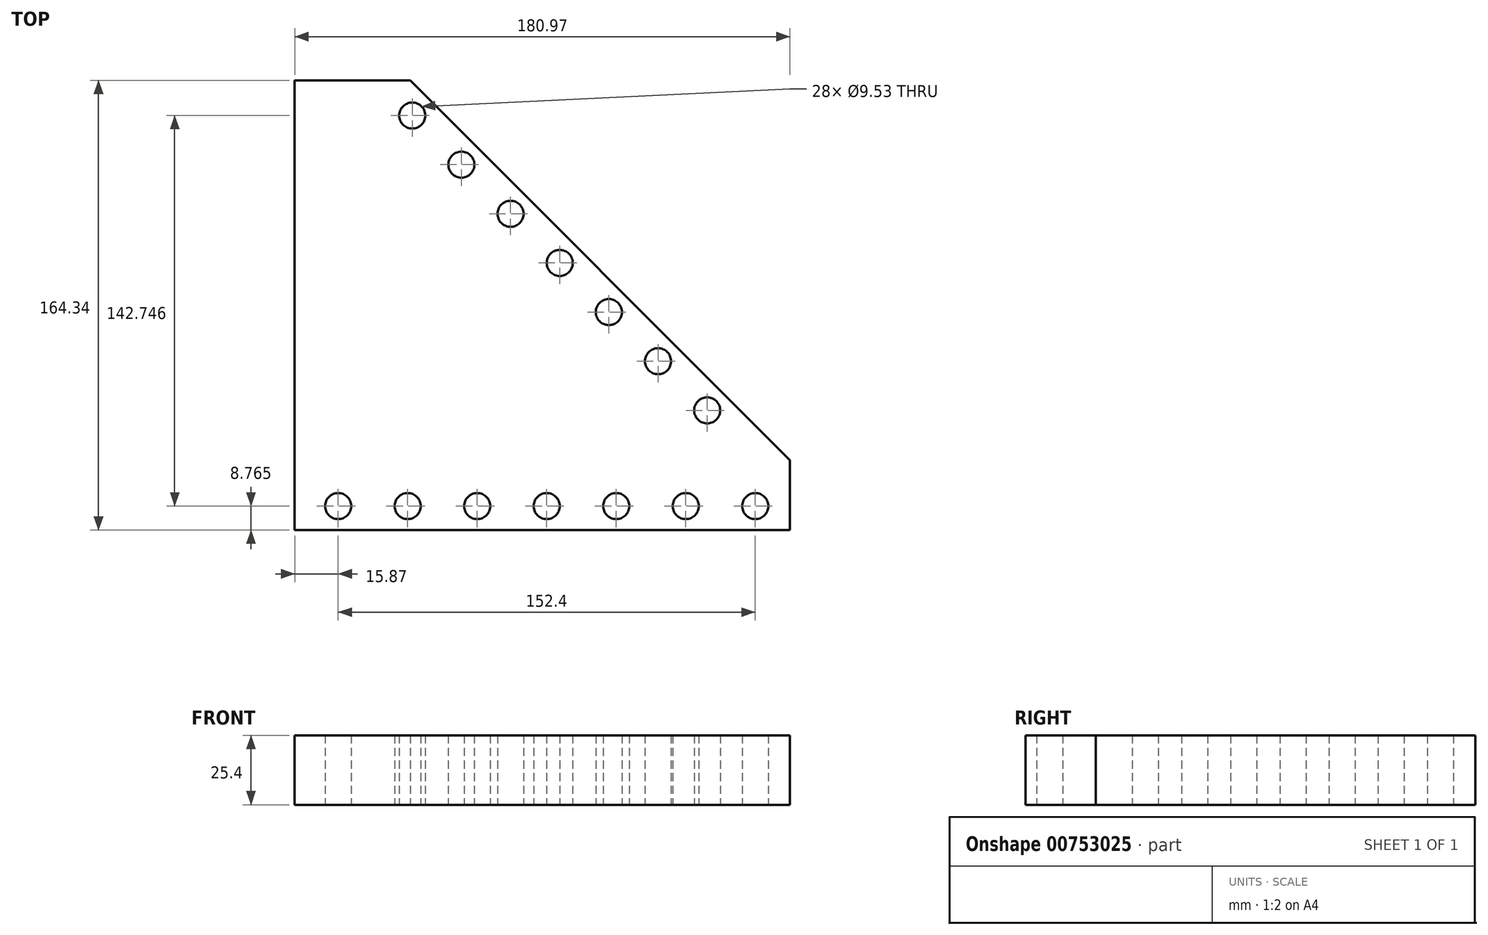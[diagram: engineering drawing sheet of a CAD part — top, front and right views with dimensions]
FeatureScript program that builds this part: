
annotation { "Feature Type Name" : "Feature", "Feature Type Description" : "" }
export const myFeature = defineFeature(function(context is Context, id is Id, definition is map)
    precondition{}
    {
        {
            var Q0;
            Q0=qCreatedBy(makeId("Top.planeOp"),FACE);
            var sketch = newSketch(context, id + "F0", { "sketchPlane" : qUnion([Q0])});
            skLineSegment(sketch, "E0.bottom", {"start": v(0, 0) * mm, "end": v(-304.8, 0) * mm});
            skLineSegment(sketch, "E0.top", {"start": v(0, 19.05) * mm, "end": v(-304.8, 19.05) * mm});
            skLineSegment(sketch, "E0.left", {"start": v(0, 0) * mm, "end": v(0, 19.05) * mm});
            skLineSegment(sketch, "E0.right", {"start": v(-304.8, 0) * mm, "end": v(-304.8, 19.05) * mm});
            skCircle(sketch, "E1", {"center": v(-25.4, 9.52) * mm, "radius": 4.76 * mm});
            skCircle(sketch, "E2.1.0.0", {"center": v(-50.8, 9.52) * mm, "radius": 4.76 * mm});
            skCircle(sketch, "E2.2.0.0", {"center": v(-76.2, 9.52) * mm, "radius": 4.76 * mm});
            skCircle(sketch, "E2.3.0.0", {"center": v(-101.6, 9.52) * mm, "radius": 4.76 * mm});
            skCircle(sketch, "E2.4.0.0", {"center": v(-127, 9.52) * mm, "radius": 4.76 * mm});
            skCircle(sketch, "E2.5.0.0", {"center": v(-152.4, 9.52) * mm, "radius": 4.76 * mm});
            skCircle(sketch, "E2.6.0.0", {"center": v(-177.8, 9.52) * mm, "radius": 4.76 * mm});
            skCircle(sketch, "E2.7.0.0", {"center": v(-203.2, 9.52) * mm, "radius": 4.76 * mm});
            skCircle(sketch, "E2.8.0.0", {"center": v(-228.6, 9.52) * mm, "radius": 4.76 * mm});
            skCircle(sketch, "E2.9.0.0", {"center": v(-254, 9.52) * mm, "radius": 4.76 * mm});
            skCircle(sketch, "E2.10.0.0", {"center": v(-279.4, 9.52) * mm, "radius": 4.76 * mm});
            skLineSegment(sketch, "E2.direction1", {"start": v(-25.4, 9.52) * mm, "end": v(-50.8, 9.52) * mm, "construction": true});
            skLineSegment(sketch, "E3.bottom", {"start": v(-57.15, 19.81) * mm, "end": v(-272.68, 235.34) * mm});
            skLineSegment(sketch, "E3.top", {"start": v(-43.68, 33.28) * mm, "end": v(-259.2, 248.8) * mm});
            skLineSegment(sketch, "E3.left", {"start": v(-57.15, 19.81) * mm, "end": v(-43.68, 33.28) * mm});
            skLineSegment(sketch, "E3.right", {"start": v(-272.68, 235.34) * mm, "end": v(-259.2, 248.8) * mm});
            skCircle(sketch, "E4", {"center": v(-68.38, 44.5) * mm, "radius": 4.76 * mm});
            skCircle(sketch, "E5.1.0.0", {"center": v(-86.34, 62.47) * mm, "radius": 4.76 * mm});
            skCircle(sketch, "E5.2.0.0", {"center": v(-104.3, 80.43) * mm, "radius": 4.76 * mm});
            skCircle(sketch, "E5.3.0.0", {"center": v(-122.26, 98.39) * mm, "radius": 4.76 * mm});
            skCircle(sketch, "E5.4.0.0", {"center": v(-140.22, 116.35) * mm, "radius": 4.76 * mm});
            skCircle(sketch, "E5.5.0.0", {"center": v(-158.18, 134.31) * mm, "radius": 4.76 * mm});
            skCircle(sketch, "E5.6.0.0", {"center": v(-176.14, 152.27) * mm, "radius": 4.76 * mm});
            skCircle(sketch, "E5.7.0.0", {"center": v(-194.1, 170.23) * mm, "radius": 4.76 * mm});
            skCircle(sketch, "E5.8.0.0", {"center": v(-212.06, 188.2) * mm, "radius": 4.76 * mm});
            skCircle(sketch, "E5.9.0.0", {"center": v(-230.02, 206.15) * mm, "radius": 4.76 * mm});
            skCircle(sketch, "E5.10.0.0", {"center": v(-247.98, 224.11) * mm, "radius": 4.76 * mm});
            skLineSegment(sketch, "E5.direction1", {"start": v(-68.38, 44.5) * mm, "end": v(-86.34, 62.47) * mm, "construction": true});
            skLineSegment(sketch, "E6.0", {"start": v(-75.11, 37.77) * mm, "end": v(-57.15, 19.81) * mm, "construction": true});
            skLineSegment(sketch, "E6.1", {"start": v(-75.11, 37.77) * mm, "end": v(-68.38, 44.5) * mm, "construction": true});
            skLineSegment(sketch, "E7", {"start": v(-38.1, 0.76) * mm, "end": v(-38.1, 26.33) * mm});
            skLineSegment(sketch, "E8", {"start": v(-219.08, 0.76) * mm, "end": v(-219.08, 165.1) * mm});
            skLineSegment(sketch, "E9", {"start": v(-219.08, 165.1) * mm, "end": v(-176.87, 165.1) * mm});
            skLineSegment(sketch, "E10", {"start": v(-219.08, 0.76) * mm, "end": v(-38.1, 0.76) * mm});
            skPoint(sketch, "E11.orphan", {"position": v(-219.08, 0) * mm});
            skPoint(sketch, "E12.orphan", {"position": v(-38.1, 0) * mm});
            skLineSegment(sketch, "E13", {"start": v(-176.87, 165.1) * mm, "end": v(-38.1, 26.33) * mm});
            skLineSegment(sketch, "E14", {"start": v(-219.08, 0.76) * mm, "end": v(-115.8, 104.03) * mm});
            skLineSegment(sketch, "E15", {"start": v(-146.95, 109.61) * mm, "end": v(-133.48, 123.08) * mm});
            skLineSegment(sketch, "E16", {"start": v(-43.68, 33.28) * mm, "end": v(-133.57, 123) * mm});
            skSolve(sketch);
        }
        {
            var Q0;
            {var subQ0=sQuery(id+"F0.wireOp",EDGE,"E8");var subQ1=sQuery(id+"F0.wireOp",EDGE,"E0.top");var subQ2=makeQuery(id+"F0.imprint","INTERSECT",VERTEX,{"derivedFrom":[subQ1,subQ0]});Q0=makeQuery(id+"F0.imprint","IMPRINT",FACE,{"disambiguationData":[TD([[makeQuery(id+"F0.imprint","IMPRINT",EDGE,{"disambiguationData":[TD([[subQ2,1.0]])],"derivedFrom":subQ1}),-1.0]])]});}
            var Q1;
            Q1=makeQuery(id+"F0.imprint","IMPRINT",FACE,{"disambiguationData":[TD([[makeQuery(id+"F0.imprint","IMPRINT",EDGE,{"derivedFrom":sQuery(id+"F0.wireOp",EDGE,"E2.2.0.0")}),-1.0]])]});
            var Q2;
            Q2=makeQuery(id+"F0.imprint","IMPRINT",FACE,{"disambiguationData":[TD([[makeQuery(id+"F0.imprint","IMPRINT",EDGE,{"derivedFrom":sQuery(id+"F0.wireOp",EDGE,"E4")}),-1.0]])]});
            var Q3;
            {var subQ0=sQuery(id+"F0.wireOp",EDGE,"E8");var subQ1=sQuery(id+"F0.wireOp",EDGE,"E0.top");var subQ2=makeQuery(id+"F0.imprint","INTERSECT",VERTEX,{"derivedFrom":[subQ1,subQ0]});Q3=makeQuery(id+"F0.imprint","IMPRINT",FACE,{"disambiguationData":[TD([[makeQuery(id+"F0.imprint","IMPRINT",EDGE,{"disambiguationData":[TD([[subQ2,1.0]])],"derivedFrom":subQ1}),1.0]])]});}
            var Q4;
            Q4=makeQuery(id+"F0.imprint","IMPRINT",FACE,{"disambiguationData":[TD([[makeQuery(id+"F0.imprint","IMPRINT",EDGE,{"derivedFrom":sQuery(id+"F0.wireOp",EDGE,"E5.4.0.0")}),-1.0]])]});
            var Q5;
            {var subQ1=sQuery(id+"F0.wireOp",EDGE,"E0.top");var subQ3=sQuery(id+"F0.wireOp",EDGE,"E14");var subQ4=makeQuery(id+"F0.imprint","INTERSECT",VERTEX,{"derivedFrom":[subQ1,subQ3]});Q5=makeQuery(id+"F0.imprint","IMPRINT",FACE,{"disambiguationData":[TD([[makeQuery(id+"F0.imprint","IMPRINT",EDGE,{"disambiguationData":[TD([[subQ4,-1.0]])],"derivedFrom":subQ3}),-1.0]])]});}
            var Q6;
            {var subQ3=sQuery(id+"F0.wireOp",EDGE,"E7");var subQ5=sQuery(id+"F0.wireOp",EDGE,"E13");var subQ7=makeQuery(id+"F0.imprint","INTERSECT",VERTEX,{"derivedFrom":[subQ3,subQ5]});Q6=makeQuery(id+"F0.imprint","IMPRINT",FACE,{"disambiguationData":[TD([[makeQuery(id+"F0.imprint","IMPRINT",EDGE,{"disambiguationData":[TD([[subQ7,1.0]])],"derivedFrom":subQ3}),1.0]])]});}
            extrude(context, id + "F1", {"entities" : qUnion([Q0, Q1, Q2, Q3, Q4, Q5, Q6]), "depth" : 25.4 * mm, "offsetDistance" : 25.4 * mm});
        }
    });
